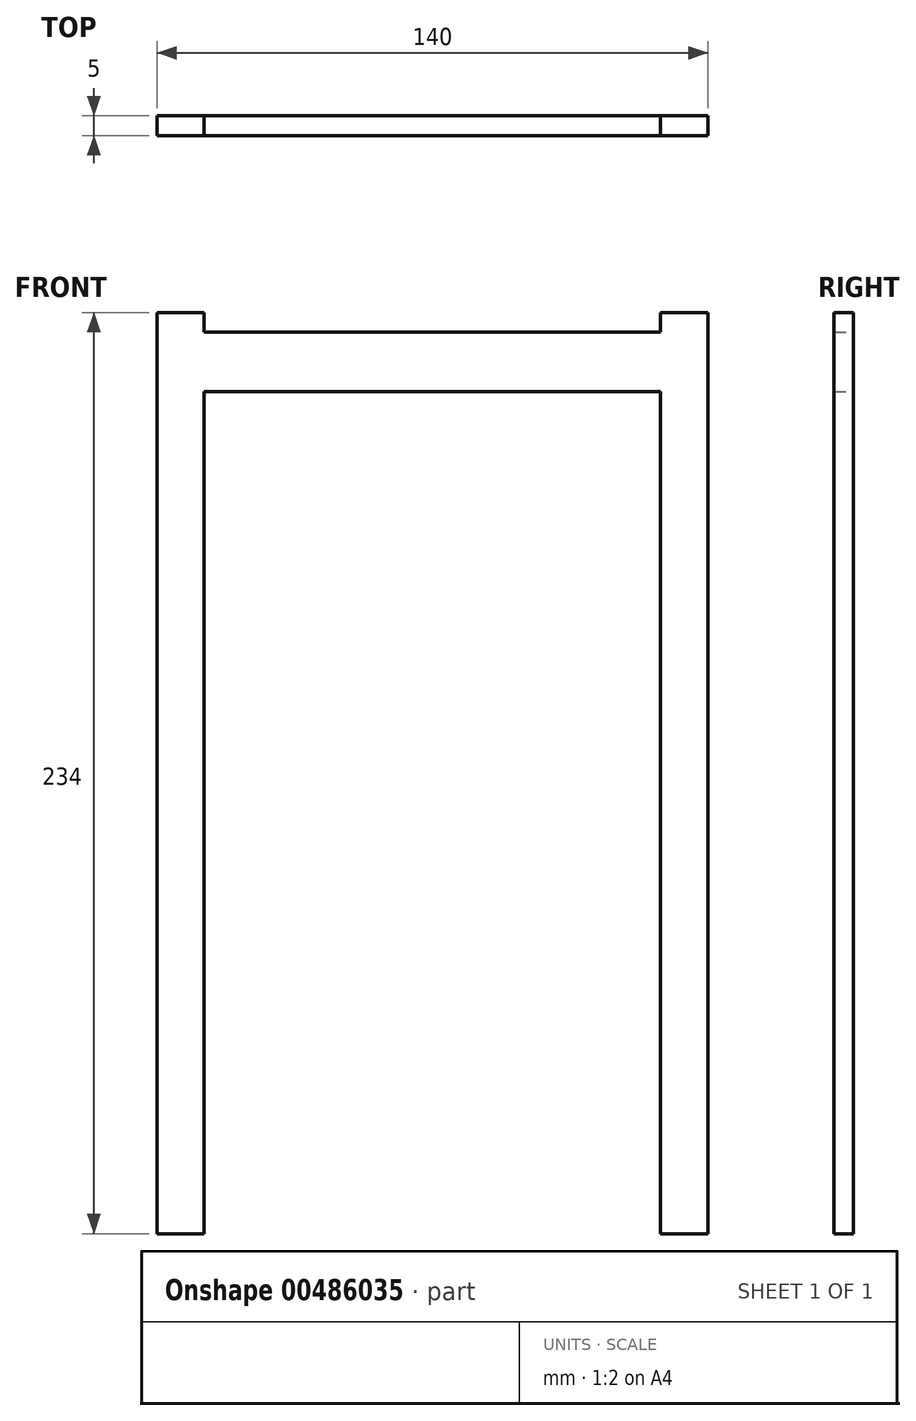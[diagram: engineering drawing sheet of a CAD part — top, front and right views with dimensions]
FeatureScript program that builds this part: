
annotation { "Feature Type Name" : "Feature", "Feature Type Description" : "" }
export const myFeature = defineFeature(function(context is Context, id is Id, definition is map)
    precondition{}
    {
        {
            var Q0;
            Q0=qCreatedBy(makeId("Front.planeOp"),FACE);
            var sketch = newSketch(context, id + "F0", { "sketchPlane" : qUnion([Q0])});
            skLineSegment(sketch, "E0.bottom", {"start": v(-70, -115.52) * mm, "end": v(-58, -115.52) * mm});
            skLineSegment(sketch, "E0.top", {"start": v(-70, 118.48) * mm, "end": v(-58, 118.48) * mm});
            skLineSegment(sketch, "E0.left", {"start": v(-70, -115.52) * mm, "end": v(-70, 118.48) * mm});
            skLineSegment(sketch, "E0.right", {"start": v(-58, -115.52) * mm, "end": v(-58, 118.48) * mm});
            skLineSegment(sketch, "E1.bottom", {"start": v(-58, 113.48) * mm, "end": v(0, 113.48) * mm});
            skLineSegment(sketch, "E1.top", {"start": v(-58, 98.48) * mm, "end": v(0, 98.48) * mm});
            skLineSegment(sketch, "E1.left", {"start": v(-58, 113.48) * mm, "end": v(-58, 98.48) * mm});
            skLineSegment(sketch, "E1.right", {"start": v(0, 113.48) * mm, "end": v(0, 98.48) * mm});
            skLineSegment(sketch, "E2.MirrorCS", {"start": v(70, 118.48) * mm, "end": v(58, 118.48) * mm});
            skLineSegment(sketch, "E3.MirrorCS", {"start": v(70, -115.52) * mm, "end": v(58, -115.52) * mm});
            skLineSegment(sketch, "E4.MirrorCS", {"start": v(58, 113.48) * mm, "end": v(58, 98.48) * mm});
            skLineSegment(sketch, "E5.MirrorCS", {"start": v(58, 98.48) * mm, "end": v(0, 98.48) * mm});
            skLineSegment(sketch, "E6.MirrorCS", {"start": v(58, 113.48) * mm, "end": v(0, 113.48) * mm});
            skLineSegment(sketch, "E7.MirrorCS", {"start": v(58, -115.52) * mm, "end": v(58, 118.48) * mm});
            skLineSegment(sketch, "E8.MirrorCS", {"start": v(70, -115.52) * mm, "end": v(70, 118.48) * mm});
            skSolve(sketch);
        }
        {
            var Q0;
            Q0=makeQuery(id+"F0.imprint","IMPRINT",FACE,{"disambiguationData":[TD([[makeQuery(id+"F0.imprint","IMPRINT",EDGE,{"derivedFrom":sQuery(id+"F0.wireOp",EDGE,"E1.bottom")}),-1.0]])]});
            var Q1;
            {var subQ1=sQuery(id+"F0.wireOp",EDGE,"E0.bottom");Q1=makeQuery(id+"F0.imprint","IMPRINT",FACE,{"disambiguationData":[TD([[makeQuery(id+"F0.imprint","IMPRINT",EDGE,{"derivedFrom":subQ1}),1.0]])]});}
            var Q2;
            Q2=makeQuery(id+"F0.imprint","IMPRINT",FACE,{"disambiguationData":[TD([[makeQuery(id+"F0.imprint","IMPRINT",EDGE,{"derivedFrom":sQuery(id+"F0.wireOp",EDGE,"E1.right")}),1.0]])]});
            var Q3;
            {var subQ4=sQuery(id+"F0.wireOp",EDGE,"E2.MirrorCS");Q3=makeQuery(id+"F0.imprint","IMPRINT",FACE,{"disambiguationData":[TD([[makeQuery(id+"F0.imprint","IMPRINT",EDGE,{"derivedFrom":subQ4}),1.0]])]});}
            extrude(context, id + "F1", {"entities" : qUnion([Q0, Q1, Q2, Q3]), "depth" : 5 * mm});
        }
    });
